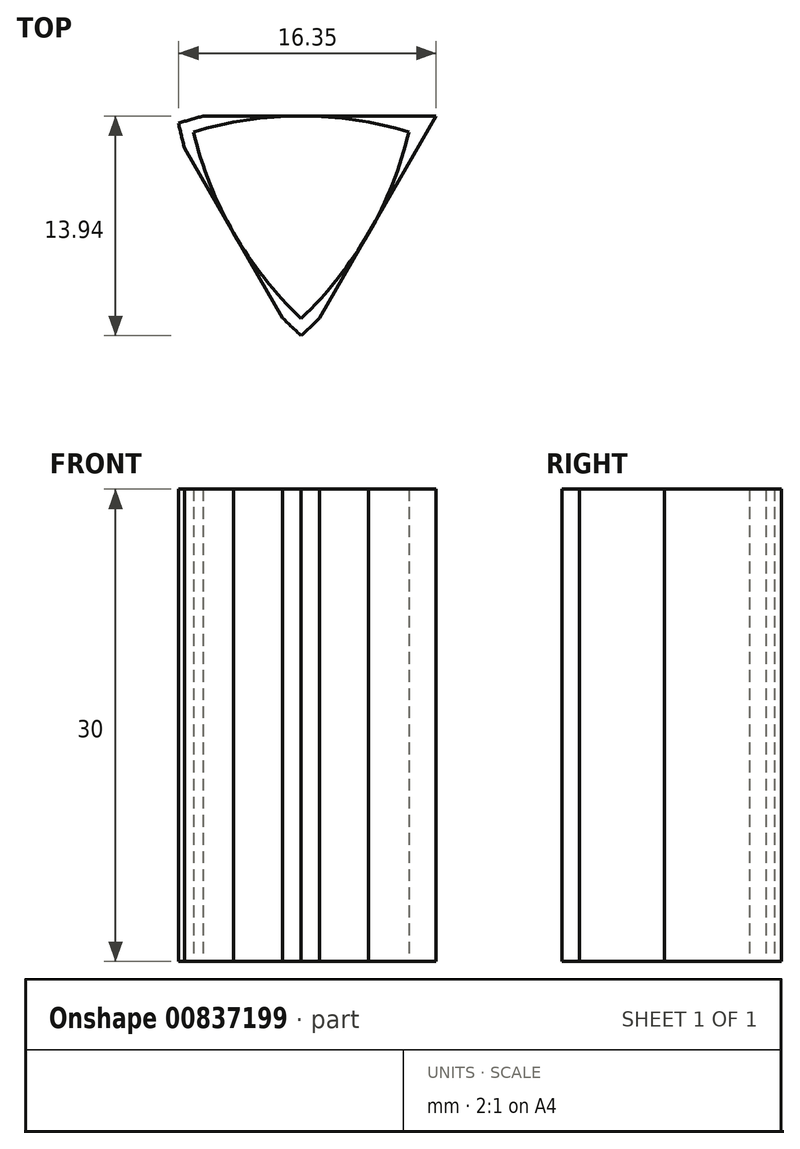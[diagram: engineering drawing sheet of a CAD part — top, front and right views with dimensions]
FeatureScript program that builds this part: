
annotation { "Feature Type Name" : "Feature", "Feature Type Description" : "" }
export const myFeature = defineFeature(function(context is Context, id is Id, definition is map)
    precondition{}
    {
        {
            var Q0;
            Q0=qCreatedBy(makeId("Top.planeOp"),FACE);
            var sketch = newSketch(context, id + "F0", { "sketchPlane" : qUnion([Q0])});
            skCircle(sketch, "E0.cCircle", {"center": v(0, 0) * mm, "radius": 4.95 * mm, "construction": true});
            skLineSegment(sketch, "E0.0", {"start": v(0, -9.9) * mm, "end": v(-8.57, 4.95) * mm});
            skLineSegment(sketch, "E0.1", {"start": v(8.57, 4.95) * mm, "end": v(-8.57, 4.95) * mm});
            skLineSegment(sketch, "E0.2", {"start": v(8.57, 4.95) * mm, "end": v(0, -9.9) * mm});
            skPoint(sketch, "E0.0.midPoint", {"position": v(-4.29, -2.48) * mm});
            skLineSegment(sketch, "E1", {"start": v(0, 0) * mm, "end": v(8.57, 4.95) * mm, "construction": true});
            skLineSegment(sketch, "E2", {"start": v(0, 0) * mm, "end": v(-8.57, 4.95) * mm, "construction": true});
            skLineSegment(sketch, "E3", {"start": v(0, 0) * mm, "end": v(0, -9.9) * mm, "construction": true});
            skArc(sketch, "E4", {"start": v(0, 4.95) * mm, "mid": v(-3.46, 4.7) * mm, "end": v(-6.84, 3.95) * mm});
            skArc(sketch, "E5.MirrorCS", {"start": v(-4.29, -2.48) * mm, "mid": v(-5.8, 0.64) * mm, "end": v(-6.84, 3.95) * mm});
            skArc(sketch, "E6.1.0", {"start": v(-4.29, -2.48) * mm, "mid": v(-2.34, -5.34) * mm, "end": v(0, -7.9) * mm});
            skArc(sketch, "E6.1.1", {"start": v(4.29, -2.48) * mm, "mid": v(2.34, -5.34) * mm, "end": v(0, -7.9) * mm});
            skArc(sketch, "E6.2.0", {"start": v(4.29, -2.48) * mm, "mid": v(5.8, 0.64) * mm, "end": v(6.84, 3.95) * mm});
            skArc(sketch, "E6.2.1", {"start": v(0, 4.95) * mm, "mid": v(3.46, 4.7) * mm, "end": v(6.84, 3.95) * mm});
            skArc(sketch, "E7.0", {"start": v(0, 5.75) * mm, "mid": v(3.94, 5.43) * mm, "end": v(7.78, 4.5) * mm});
            skArc(sketch, "E7.1", {"start": v(-4.98, -2.88) * mm, "mid": v(-6.68, 0.7) * mm, "end": v(-7.78, 4.5) * mm});
            skArc(sketch, "E7.2", {"start": v(-4.98, -2.88) * mm, "mid": v(-2.74, -6.13) * mm, "end": v(0, -8.99) * mm});
            skArc(sketch, "E7.3", {"start": v(0, 5.75) * mm, "mid": v(-3.94, 5.43) * mm, "end": v(-7.78, 4.5) * mm});
            skArc(sketch, "E7.4", {"start": v(4.98, -2.88) * mm, "mid": v(2.74, -6.13) * mm, "end": v(0, -8.99) * mm});
            skArc(sketch, "E7.5", {"start": v(4.98, -2.88) * mm, "mid": v(6.68, 0.7) * mm, "end": v(7.78, 4.5) * mm});
            skSolve(sketch);
        }
        {
            var Q0;
            Q0=makeQuery(id+"F0.imprint","IMPRINT",FACE,{"disambiguationData":[TD([[makeQuery(id+"F0.imprint","IMPRINT",EDGE,{"derivedFrom":sQuery(id+"F0.wireOp",EDGE,"E7.0")}),-1.0]])]});
            var Q1;
            {var subQ4=sQuery(id+"F0.wireOp",EDGE,"E4");Q1=makeQuery(id+"F0.imprint","IMPRINT",FACE,{"disambiguationData":[TD([[makeQuery(id+"F0.imprint","IMPRINT",EDGE,{"derivedFrom":subQ4}),-1.0]])]});}
            var Q2;
            {var subQ4=sQuery(id+"F0.wireOp",EDGE,"E6.2.0");Q2=makeQuery(id+"F0.imprint","IMPRINT",FACE,{"disambiguationData":[TD([[makeQuery(id+"F0.imprint","IMPRINT",EDGE,{"derivedFrom":subQ4}),-1.0]])]});}
            var Q3;
            {var subQ3=sQuery(id+"F0.wireOp",EDGE,"E6.1.0");Q3=makeQuery(id+"F0.imprint","IMPRINT",FACE,{"disambiguationData":[TD([[makeQuery(id+"F0.imprint","IMPRINT",EDGE,{"derivedFrom":subQ3}),-1.0]])]});}
            var Q4;
            {var subQ2=sQuery(id+"F0.wireOp",EDGE,"E7.2");var subQ4=sQuery(id+"F0.wireOp",EDGE,"E7.1");var subQ6=makeQuery(id+"F0.imprint","INTERSECT",VERTEX,{"derivedFrom":[subQ4,subQ2]});Q4=makeQuery(id+"F0.imprint","IMPRINT",FACE,{"disambiguationData":[TD([[makeQuery(id+"F0.imprint","IMPRINT",EDGE,{"disambiguationData":[TD([[subQ6,-1.0]])],"derivedFrom":subQ4}),-1.0]])]});}
            var Q5;
            {var subQ2=sQuery(id+"F0.wireOp",EDGE,"E7.5");var subQ4=sQuery(id+"F0.wireOp",EDGE,"E7.4");var subQ6=makeQuery(id+"F0.imprint","INTERSECT",VERTEX,{"derivedFrom":[subQ4,subQ2]});Q5=makeQuery(id+"F0.imprint","IMPRINT",FACE,{"disambiguationData":[TD([[makeQuery(id+"F0.imprint","IMPRINT",EDGE,{"disambiguationData":[TD([[subQ6,-1.0]])],"derivedFrom":subQ4}),-1.0]])]});}
            extrude(context, id + "F1", {"entities" : qUnion([Q0, Q1, Q2, Q3, Q4, Q5]), "depth" : 30 * mm, "offsetDistance" : 25 * mm});
        }
    });
